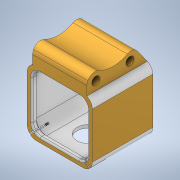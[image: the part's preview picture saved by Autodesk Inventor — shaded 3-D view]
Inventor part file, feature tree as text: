
AUTODESK INVENTOR PART (.ipt)
format: ipt  version: 2020 (Build 240168000, 168)  size: 286,208 bytes
history: native  units: in
note: dims shown in document units (in); Inventor stores cm internally (conversion verified against a paired STEP export)
features: extrude x4, sketch x4, other x3, projected_geometry x3, fillet x2
ambient origin geometry x8: Origin, YZ Plane, XZ Plane, XY Plane, X Axis, Y Axis, Z Axis, Center Point
bodies: Solid1 (feature_tree)
feature tree (16):
  other  "Assembly4.iam"
  other  "Kauri modular session 5 mount.ipt:1"
  other  "session 5.ipt:1"
  extrude  "Extrusion1"  Depth=1.0in TaperAngle=0.0deg
  extrude  "Extrusion2"  Depth=1.0in TaperAngle=0.0deg
  extrude  "Extrusion3"  Depth=0.0394in TaperAngle=0.0deg
  fillet  "Fillet1"  Radius=0.2362in
  fillet  "Fillet2"  Radius=0.0394in
  extrude  "Extrusion4"  Depth=0.0197in
  sketch  "Sketch1"  dims[d0=0.3937in d1=1.0in d2=0.0in]
  projected_geometry  "Projected Loop1"
  sketch  "Sketch2"  dims[d3=0.5906in d4=1.0in d5=0.0in]
  sketch  "Sketch3"  dims[d6=0.9843in d7=0.3937in d8=0.0in d9=0.2362in d10=0.0394in]
  projected_geometry  "Projected Loop2"
  sketch  "Sketch4"  dims[d12=0.0197in d15=0.3937in d16=0.0in d17=0.0197in d18=0.0197in d19=0.0197in d20=0.0197in]
  projected_geometry  "Projected Loop3"
